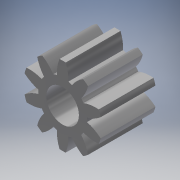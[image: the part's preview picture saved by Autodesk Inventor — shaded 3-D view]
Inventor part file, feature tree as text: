
AUTODESK INVENTOR PART (.ipt)
format: ipt  version: 2019 (Build 230136000, 136)  size: 197,120 bytes
history: native  units: mm (DEFAULTED — no unit token found)
features: plane x3, other x3, sketch x3, extrude x1, hole x1
ambient origin geometry x8: Origin, YZ Plane, XZ Plane, XY Plane, X Axis, Y Axis, Z Axis, Center Point
bodies: Solid1 (feature_tree)
feature tree (11):
  extrude  "Extrusion1"  Depth=4.2mm TaperAngle=0.0deg
  plane  "Work Plane2"
  plane  "Work Plane8"
  plane  "Work Plane9"
  other  "Przekładnia walcowa"
  hole  "Otwór1"  [1 undecoded]
  sketch  "Sketch1"  dims[d0=6.0mm d1=4.2mm d2=0.0mm]
  sketch  "Sketch2"  dims[d3=5.0mm d4=10.0mm d5=0.0mm d16=8.75mm d17=0.0mm d34=3.141593mm d39=0.0mm d41=0.0mm d43=8.75mm d46=8.75mm d47=0.0mm d48=0.0mm d49=2.5mm d50=6.0mm d51=4.0mm d52=2.0mm d53=90.0deg d54=8.0mm d55=20.594885mm]
  other  "Srf1"
  sketch  "Szkic3"
  other  "Średnica podziałowa"
note: 1 required parameter value undecoded (feature->parameter linkage not recoverable at this tier; creation-order binding heuristic only, values carry confidence <= 0.55)
